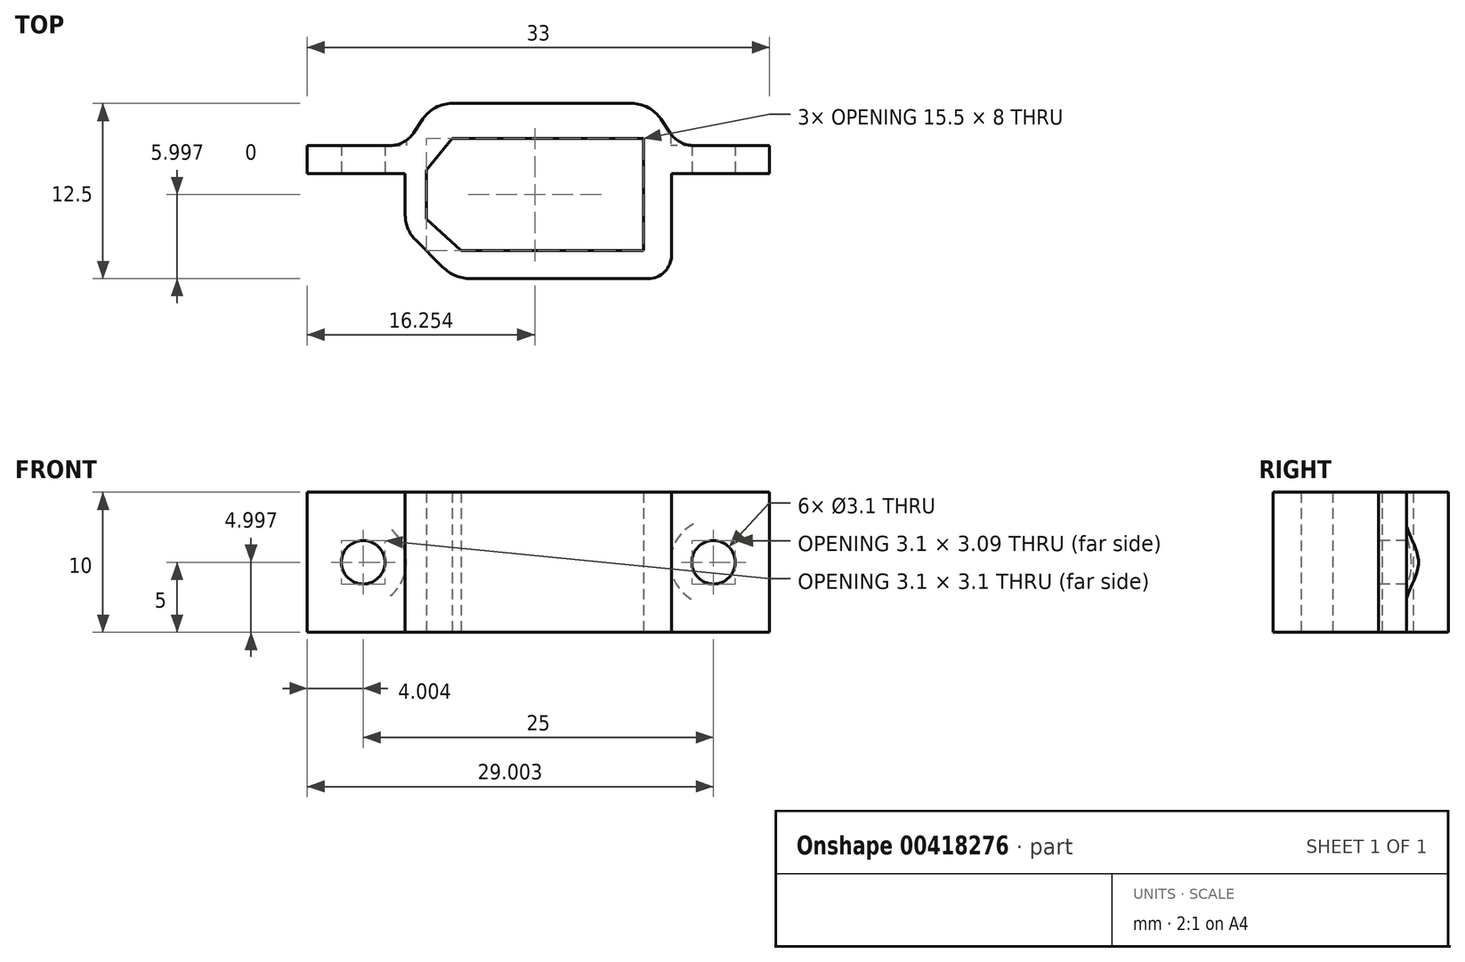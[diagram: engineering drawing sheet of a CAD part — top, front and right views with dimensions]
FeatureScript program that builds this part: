
annotation { "Feature Type Name" : "Feature", "Feature Type Description" : "" }
export const myFeature = defineFeature(function(context is Context, id is Id, definition is map)
    precondition{}
    {
        {
            var Q0;
            Q0=qCreatedBy(makeId("Top.planeOp"),FACE);
            var sketch = newSketch(context, id + "F0", { "sketchPlane" : qUnion([Q0])});
            skLineSegment(sketch, "E0", {"start": v(-6.5, 14.3) * mm, "end": v(-1.57, 14.3) * mm});
            skLineSegment(sketch, "E1", {"start": v(-1.57, 12.3) * mm, "end": v(-7.57, 12.3) * mm});
            skLineSegment(sketch, "E2", {"start": v(-7.57, 12.3) * mm, "end": v(-7.57, 6.48) * mm});
            skLineSegment(sketch, "E3", {"start": v(-9.24, 4.8) * mm, "end": v(-21.92, 4.8) * mm});
            skLineSegment(sketch, "E4", {"start": v(-26.57, 9.32) * mm, "end": v(-26.57, 12.3) * mm});
            skLineSegment(sketch, "E5", {"start": v(-26.57, 12.3) * mm, "end": v(-32.57, 12.3) * mm});
            skLineSegment(sketch, "E6", {"start": v(-32.57, 14.3) * mm, "end": v(-27.64, 14.3) * mm});
            skLineSegment(sketch, "E7", {"start": v(-23.23, 17.3) * mm, "end": v(-10.4, 17.3) * mm});
            skLineSegment(sketch, "E8", {"start": v(-23.87, 5.62) * mm, "end": v(-25.85, 7.59) * mm});
            skLineSegment(sketch, "E9", {"start": v(-25.3, 16.2) * mm, "end": v(-25.97, 15.2) * mm});
            skLineSegment(sketch, "E10", {"start": v(-7.66, 15.2) * mm, "end": v(-8.32, 16.2) * mm});
            skPoint(sketch, "E11.orphan", {"position": v(-7.57, 17.3) * mm});
            skPoint(sketch, "E12.visualSharp", {"position": v(-7.57, 4.8) * mm});
            skArc(sketch, "E12.filletArc", {"start": v(-9.24, 4.8) * mm, "mid": v(-8.06, 5.3) * mm, "end": v(-7.57, 6.48) * mm});
            skPoint(sketch, "E13.visualSharp", {"position": v(-23.07, 4.8) * mm});
            skArc(sketch, "E13.filletArc", {"start": v(-23.87, 5.62) * mm, "mid": v(-22.98, 5.02) * mm, "end": v(-21.92, 4.8) * mm});
            skPoint(sketch, "E14.visualSharp", {"position": v(-26.57, 8.3) * mm});
            skArc(sketch, "E14.filletArc", {"start": v(-26.57, 9.32) * mm, "mid": v(-26.38, 8.38) * mm, "end": v(-25.85, 7.59) * mm});
            skPoint(sketch, "E15.visualSharp", {"position": v(-7.57, 14.3) * mm});
            skArc(sketch, "E15.filletArc", {"start": v(-7.66, 15.2) * mm, "mid": v(-6.94, 14.54) * mm, "end": v(-6, 14.3) * mm});
            skPoint(sketch, "E16.visualSharp", {"position": v(-26.57, 14.3) * mm});
            skArc(sketch, "E16.filletArc", {"start": v(-27.64, 14.3) * mm, "mid": v(-26.7, 14.54) * mm, "end": v(-25.97, 15.2) * mm});
            skPoint(sketch, "E17.visualSharp", {"position": v(-24.57, 17.3) * mm});
            skArc(sketch, "E17.filletArc", {"start": v(-23.23, 17.3) * mm, "mid": v(-24.4, 17.01) * mm, "end": v(-25.3, 16.2) * mm});
            skPoint(sketch, "E18.visualSharp", {"position": v(-9.57, 17.3) * mm});
            skArc(sketch, "E18.filletArc", {"start": v(-8.32, 16.2) * mm, "mid": v(-9.22, 17.01) * mm, "end": v(-10.4, 17.3) * mm});
            skLineSegment(sketch, "E19", {"start": v(-9.57, 17.3) * mm, "end": v(-9.57, 16.92) * mm});
            skLineSegment(sketch, "E20", {"start": v(-9.57, 6.8) * mm, "end": v(-22.57, 6.8) * mm});
            skLineSegment(sketch, "E21", {"start": v(-25.07, 9.06) * mm, "end": v(-25.07, 12.56) * mm});
            skLineSegment(sketch, "E22", {"start": v(-23.23, 14.8) * mm, "end": v(-9.57, 14.8) * mm});
            skLineSegment(sketch, "E23.trimOffspring", {"start": v(-9.57, 14.8) * mm, "end": v(-9.57, 6.8) * mm});
            skLineSegment(sketch, "E24", {"start": v(-25.07, 10.8) * mm, "end": v(-25.07, 12.56) * mm});
            skLineSegment(sketch, "E25", {"start": v(-25.07, 12.56) * mm, "end": v(-25.07, 9.06) * mm});
            skLineSegment(sketch, "E26", {"start": v(-9.57, 14.8) * mm, "end": v(-22.57, 14.8) * mm});
            skLineSegment(sketch, "E27", {"start": v(-23.23, 14.8) * mm, "end": v(-25.07, 12.56) * mm});
            skLineSegment(sketch, "E28", {"start": v(-25.07, 9.06) * mm, "end": v(-22.57, 6.8) * mm});
            skPoint(sketch, "E29.orphan", {"position": v(-25.07, 6.8) * mm});
            skPoint(sketch, "E30.orphan", {"position": v(-25.07, 14.8) * mm});
            skPoint(sketch, "E31.start.orphan", {"position": v(-9.57, 10.8) * mm});
            skLineSegment(sketch, "E32", {"start": v(-1.57, 12.3) * mm, "end": v(-0.57, 12.3) * mm});
            skLineSegment(sketch, "E33", {"start": v(-0.57, 12.3) * mm, "end": v(-0.57, 14.3) * mm});
            skLineSegment(sketch, "E34", {"start": v(-0.57, 14.3) * mm, "end": v(-1.57, 14.3) * mm});
            skLineSegment(sketch, "E35", {"start": v(-32.57, 14.3) * mm, "end": v(-33.57, 14.3) * mm});
            skLineSegment(sketch, "E36", {"start": v(-33.57, 14.3) * mm, "end": v(-33.57, 12.3) * mm});
            skLineSegment(sketch, "E37", {"start": v(-33.57, 12.3) * mm, "end": v(-32.57, 12.3) * mm});
            skSolve(sketch);
        }
        {
            var Q0;
            Q0=makeQuery(id+"F0.imprint","IMPRINT",FACE,{"disambiguationData":[TD([[makeQuery(id+"F0.imprint","IMPRINT",EDGE,{"derivedFrom":sQuery(id+"F0.wireOp",EDGE,"E0")}),-1.0]])]});
            var Q1;
            Q1 = qSketchRegion(id + "F2", true);
            extrude(context, id + "F1", {"entities" : qUnion([Q0, Q1]), "depth" : 10 * mm});
        }
        {
            var Q0;
            Q0=makeQuery(id+"F1.opExtrude","SWEPT_FACE",FACE,{"disambiguationData":[OSD([sQuery(id+"F0.wireOp",EDGE,"E5")])]});
            var sketch = newSketch(context, id + "F2", { "sketchPlane" : qUnion([Q0])});
            skLineSegment(sketch, "E38.bottom", {"start": v(-26.57, 10) * mm, "end": v(4.43, 10) * mm});
            skLineSegment(sketch, "E38.top", {"start": v(-26.57, 0) * mm, "end": v(4.43, 0) * mm});
            skLineSegment(sketch, "E38.left", {"start": v(-26.57, 10) * mm, "end": v(-26.57, 0) * mm});
            skLineSegment(sketch, "E38.right", {"start": v(4.43, 10) * mm, "end": v(4.43, 0) * mm});
            skLineSegment(sketch, "E39", {"start": v(-26.57, 10) * mm, "end": v(-26.57, 5) * mm});
            skPoint(sketch, "E40.endSnap0", {"position": v(4.43, 5) * mm});
            skCircle(sketch, "E41", {"center": v(-29.57, 5) * mm, "radius": 1.55 * mm});
            skCircle(sketch, "E42", {"center": v(-4.57, 5) * mm, "radius": 1.55 * mm});
            skPoint(sketch, "E40.end.orphan", {"position": v(4.43, 5) * mm});
            skSolve(sketch);
        }
        {
            var Q0;
            Q0=makeQuery(id+"F2.imprint","IMPRINT",FACE,{"disambiguationData":[TD([[makeQuery(id+"F2.imprint","IMPRINT",EDGE,{"derivedFrom":sQuery(id+"F2.wireOp",EDGE,"E41")}),1.0]])]});
            var Q1;
            Q1=makeQuery(id+"F2.imprint","IMPRINT",FACE,{"disambiguationData":[TD([[makeQuery(id+"F2.imprint","IMPRINT",EDGE,{"derivedFrom":sQuery(id+"F2.wireOp",EDGE,"E42")}),1.0]])]});
            extrude(context, id + "F3", {"entities" : qUnion([Q0, Q1]), "operationType" : NewBodyOperationType.REMOVE, "oppositeDirection" : true, "depth" : 5 * mm});
        }
        {
            var Q0;
            Q0=makeQuery(id+"F1.opExtrude","SWEPT_FACE",FACE,{"disambiguationData":[OSD([sQuery(id+"F0.wireOp",EDGE,"E6")])]});
            var sketch = newSketch(context, id + "F4", { "sketchPlane" : qUnion([Q0])});
            skCircle(sketch, "E43", {"center": v(29.57, 5) * mm, "radius": 3.08 * mm});
            skSolve(sketch);
        }
        {
            var Q0;
            Q0 = qSketchRegion(id + "F4", true);
            extrude(context, id + "F5", {"entities" : qUnion([Q0]), "operationType" : NewBodyOperationType.REMOVE, "oppositeDirection" : true, "depth" : -5 * mm});
        }
        {
            var Q0;
            Q0=makeQuery(id+"F1.opExtrude","SWEPT_FACE",FACE,{"disambiguationData":[OSD([sQuery(id+"F0.wireOp",EDGE,"E0")])]});
            var sketch = newSketch(context, id + "F6", { "sketchPlane" : qUnion([Q0])});
            skCircle(sketch, "E44", {"center": v(4.57, 5) * mm, "radius": 3.08 * mm});
            skSolve(sketch);
        }
        {
            var Q0;
            Q0 = qSketchRegion(id + "F6", true);
            extrude(context, id + "F7", {"entities" : qUnion([Q0]), "operationType" : NewBodyOperationType.REMOVE, "oppositeDirection" : true, "depth" : -5 * mm});
        }
    });
